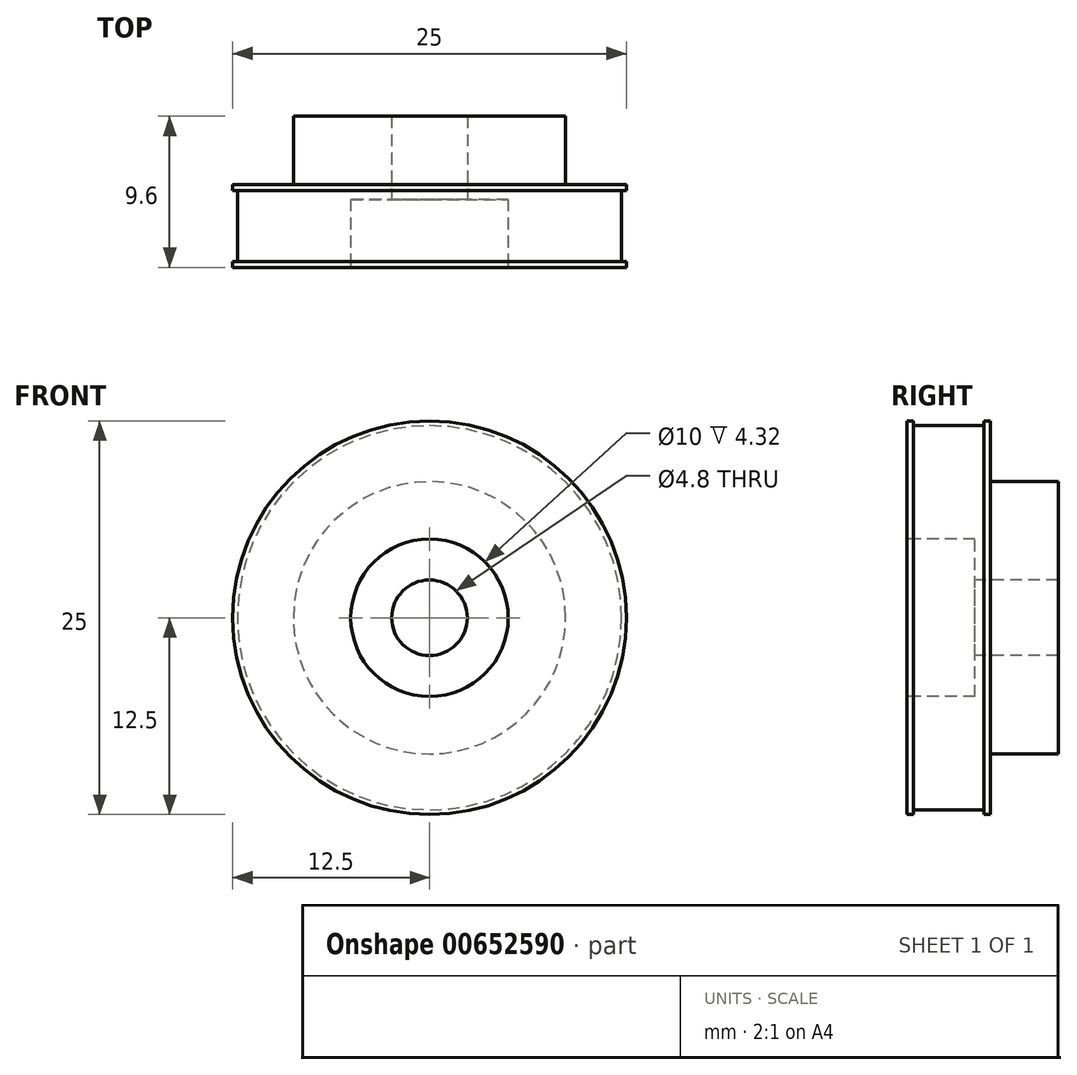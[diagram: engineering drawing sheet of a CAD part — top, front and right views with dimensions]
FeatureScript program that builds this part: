
annotation { "Feature Type Name" : "Feature", "Feature Type Description" : "" }
export const myFeature = defineFeature(function(context is Context, id is Id, definition is map)
    precondition{}
    {
        {
            var Q0;
            Q0=qCreatedBy(makeId("Front.planeOp"),FACE);
            var sketch = newSketch(context, id + "F0", { "sketchPlane" : qUnion([Q0])});
            skCircle(sketch, "E0", {"center": v(0, 0) * mm, "radius": 12.5 * mm});
            skSolve(sketch);
        }
        {
            var Q0;
            Q0 = qSketchRegion(id + "F0", true);
            extrude(context, id + "F1", {"entities" : qUnion([Q0]), "depth" : 5.28 * mm, "offsetDistance" : 25 * mm});
        }
        {
            var Q0;
            Q0=makeQuery(id+"F1.opExtrude","CAP_FACE",FACE,{"disambiguationData":[OSD([sQuery(id+"F0.wireOp",EDGE,"E0")])],"isStart":true});
            var sketch = newSketch(context, id + "F2", { "sketchPlane" : qUnion([Q0])});
            skCircle(sketch, "E1", {"center": v(0, 0) * mm, "radius": 8.65 * mm});
            skSolve(sketch);
        }
        {
            var Q0;
            Q0 = qSketchRegion(id + "F2", true);
            extrude(context, id + "F3", {"entities" : qUnion([Q0]), "operationType" : NewBodyOperationType.ADD, "depth" : 4.32 * mm, "offsetDistance" : 25 * mm});
        }
        {
            var Q0;
            Q0=makeQuery(id+"F1.opExtrude","CAP_FACE",FACE,{"disambiguationData":[OSD([sQuery(id+"F0.wireOp",EDGE,"E0")])],"isStart":false});
            var sketch = newSketch(context, id + "F4", { "sketchPlane" : qUnion([Q0])});
            skCircle(sketch, "E2", {"center": v(0, 0) * mm, "radius": 5 * mm});
            skSolve(sketch);
        }
        {
            var Q0;
            Q0 = qSketchRegion(id + "F4", true);
            extrude(context, id + "F5", {"entities" : qUnion([Q0]), "operationType" : NewBodyOperationType.REMOVE, "oppositeDirection" : true, "depth" : 4.32 * mm, "offsetDistance" : 25 * mm});
        }
        {
            var Q0;
            Q0=qCreatedBy(makeId("Right.planeOp"),FACE);
            var sketch = newSketch(context, id + "F6", { "sketchPlane" : qUnion([Q0])});
            skLineSegment(sketch, "E3.bottom", {"start": v(-0.39, 12.5) * mm, "end": v(-4.9, 12.5) * mm});
            skLineSegment(sketch, "E3.top", {"start": v(-0.39, 12.2) * mm, "end": v(-4.9, 12.2) * mm});
            skLineSegment(sketch, "E3.left", {"start": v(-0.39, 12.5) * mm, "end": v(-0.39, 12.2) * mm});
            skLineSegment(sketch, "E3.right", {"start": v(-4.9, 12.5) * mm, "end": v(-4.9, 12.2) * mm});
            skSolve(sketch);
        }
        {
            var Q0;
            Q0 = qSketchRegion(id + "F6", true);
            var Q1;
            Q1=makeQuery(id+"F1.opExtrude","SWEPT_FACE",FACE,{"disambiguationData":[OSD([sQuery(id+"F0.wireOp",EDGE,"E0")])]});
            revolve(context, id + "F7", {"operationType" : NewBodyOperationType.REMOVE, "entities" : qUnion([Q0]), "axis" : qUnion([Q1]), "revolveType" : RevolveType.FULL, "oppositeDirection" : true});
        }
        {
            var Q0;
            Q0=makeQuery(id+"F5.boolean.opBoolean","COPY",FACE,{"derivedFrom":makeQuery(id+"F5.opExtrude","CAP_FACE",FACE,{"disambiguationData":[OSD([sQuery(id+"F4.wireOp",EDGE,"E2")])],"isStart":false})});
            var sketch = newSketch(context, id + "F8", { "sketchPlane" : qUnion([Q0])});
            skCircle(sketch, "E4", {"center": v(0, 0) * mm, "radius": 2.4 * mm});
            skSolve(sketch);
        }
        {
            var Q0;
            Q0 = qSketchRegion(id + "F8", true);
            extrude(context, id + "F9", {"entities" : qUnion([Q0]), "operationType" : NewBodyOperationType.REMOVE, "oppositeDirection" : true, "depth" : 25 * mm, "offsetDistance" : 25 * mm});
        }
    });
